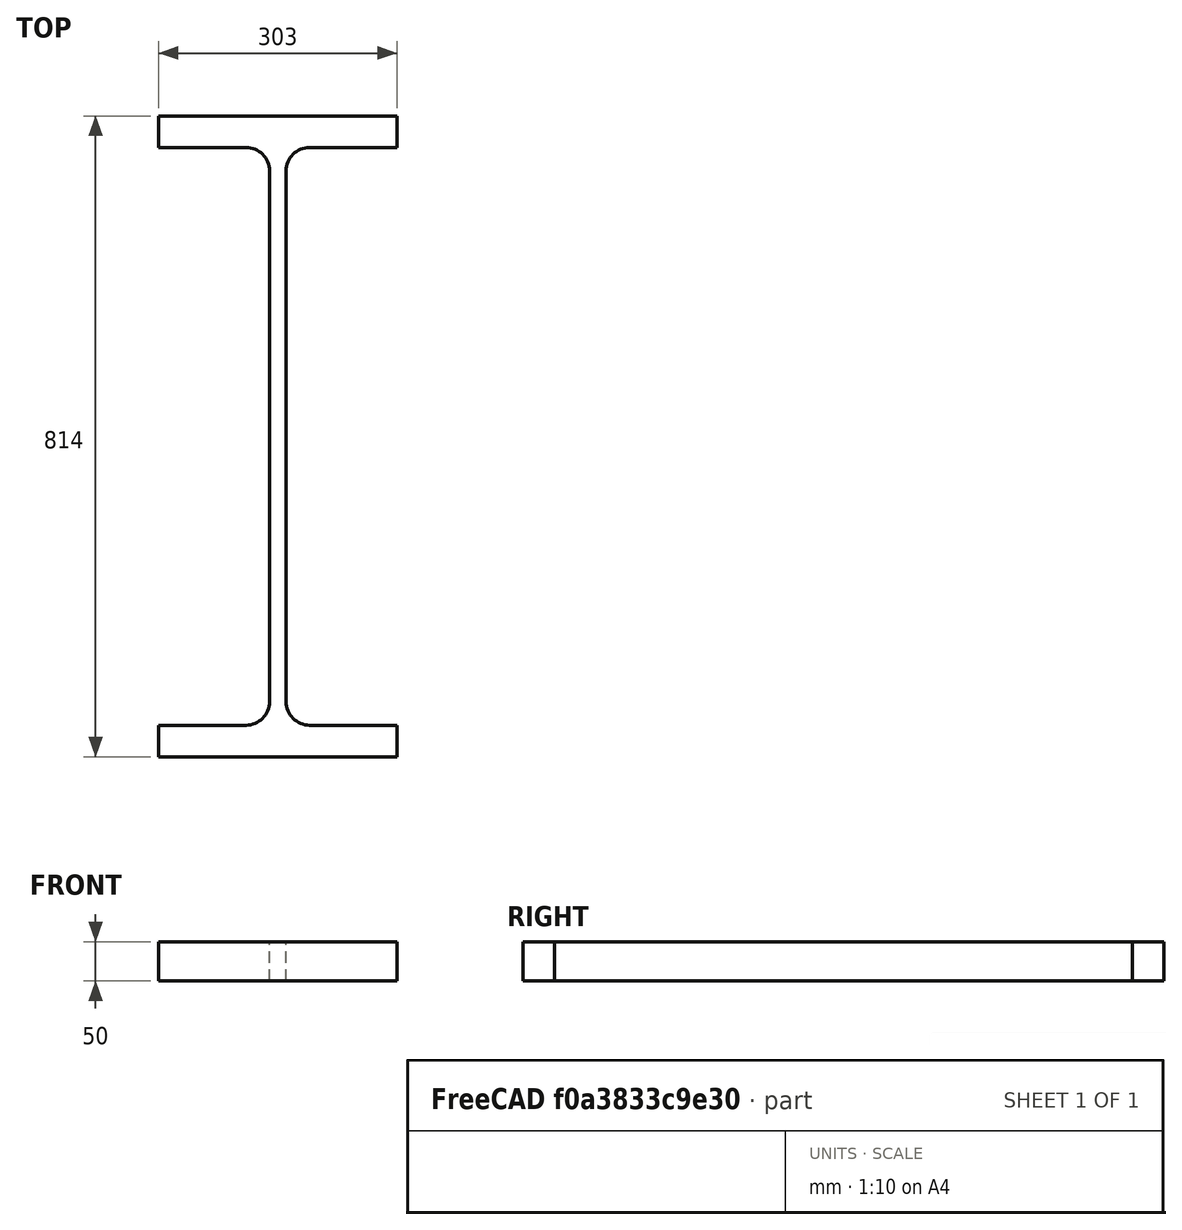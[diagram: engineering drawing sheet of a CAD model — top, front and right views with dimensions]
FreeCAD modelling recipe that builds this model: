
FCSTD DOCUMENT  (FreeCAD 0.15R4671 (Git))
Label: HE-M-Profile 800 DIN1025-4 S235JR
License: All rights reserved
LicenseURL: http://en.wikipedia.org/wiki/All_rights_reserved
objects: Sketcher::SketchObject×1, Part::Extrusion×1
note: 2 computed .brp shape members not serialized (recipe doc carries the construction recipe); baked Part::Feature solids carry a one-line shape summary decoded from their .brp

FEATURE [Sketcher::SketchObject] Sketch
  sketch-geometry (16):
    g0: LineSegment StartX=10.5 StartY=-337 StartZ=0 EndX=10.5 EndY=337 EndZ=0
    g1: LineSegment StartX=40.5 StartY=367 StartZ=0 EndX=151.5 EndY=367 EndZ=0
    g2: LineSegment StartX=151.5 StartY=367 StartZ=0 EndX=151.5 EndY=407 EndZ=0
    g3: LineSegment StartX=151.5 StartY=407 StartZ=0 EndX=-151.5 EndY=407 EndZ=0
    g4: LineSegment StartX=-151.5 StartY=407 StartZ=0 EndX=-151.5 EndY=367 EndZ=0
    g5: LineSegment StartX=-151.5 StartY=367 StartZ=0 EndX=-40.5 EndY=367 EndZ=0
    g6: LineSegment StartX=-10.5 StartY=337 StartZ=0 EndX=-10.5 EndY=-337 EndZ=0
    g7: LineSegment StartX=-40.5 StartY=-367 StartZ=0 EndX=-151.5 EndY=-367 EndZ=0
    g8: LineSegment StartX=-151.5 StartY=-367 StartZ=0 EndX=-151.5 EndY=-407 EndZ=0
    g9: LineSegment StartX=-151.5 StartY=-407 StartZ=0 EndX=151.5 EndY=-407 EndZ=0
    g10: LineSegment StartX=151.5 StartY=-407 StartZ=0 EndX=151.5 EndY=-367 EndZ=0
    g11: LineSegment StartX=151.5 StartY=-367 StartZ=0 EndX=40.5 EndY=-367 EndZ=0
    g12: ArcOfCircle CenterX=40.5 CenterY=337 CenterZ=0 NormalX=0 NormalY=0 NormalZ=1 Radius=30 StartAngle=1.5708 EndAngle=3.14159
    g13: ArcOfCircle CenterX=40.5 CenterY=-337 CenterZ=0 NormalX=0 NormalY=0 NormalZ=1 Radius=30 StartAngle=3.14159 EndAngle=4.71239
    g14: ArcOfCircle CenterX=-40.5 CenterY=337 CenterZ=0 NormalX=0 NormalY=0 NormalZ=1 Radius=30 StartAngle=0 EndAngle=1.5708
    g15: ArcOfCircle CenterX=-40.5 CenterY=-337 CenterZ=0 NormalX=0 NormalY=0 NormalZ=1 Radius=30 StartAngle=4.71239 EndAngle=6.28319
  constraints (42):
    c: Vertical(g0)
    c: Coincident(g2,g1)
    c: Vertical(g2)
    c: Coincident(g3,g2)
    c: Coincident(g4,g3)
    c: Vertical(g4)
    c: Coincident(g5,g4)
    c: Horizontal(g5)
    c: Vertical(g6)
    c: Horizontal(g7)
    c: Coincident(g8,g7)
    c: Vertical(g8)
    c: Coincident(g9,g8)
    c: Horizontal(g9)
    c: Coincident(g10,g9)
    c: Vertical(g10)
    c: Coincident(g11,g10)
    c: Horizontal(g11)
    c: Tangent(g1,g12) = 1.5708
    c: Tangent(g0,g12) = 1.5708
    c: Tangent(g0,g13) = 1.5708
    c: Tangent(g11,g13) = 1.5708
    c: Tangent(g5,g14) = 1.5708
    c: Tangent(g6,g14) = 1.5708
    c: Tangent(g6,g15) = 1.5708
    c: Tangent(g7,g15) = 1.5708
    c: Equal(g3,g9)
    c: Equal(g2,g4)
    c: Equal(g4,g8)
    c: Equal(g8,g10)
    c: Equal(g12,g14)
    c: Equal(g14,g15)
    c: Equal(g15,g13)
    c: Symmetric(g2,g3,g-2)
    c: Symmetric(g9,g8,g-2)
    c: Symmetric(g0,g6,g-2)
    c: Symmetric(g2,g9,g-1)
    c: DistanceY(g2,g9) = -814
    c: DistanceX(g3) = -303
    c: DistanceX(g0,g6) = -21
    c: DistanceY(g2) = 40
    c: Radius(g12) = 30
FEATURE [Part::Extrusion] Extrude  label="HE-M-Profile 800 DIN1025-4 S235JR"
  Base = -> Sketch
  Dir = (0,0,50)
  Solid = true
